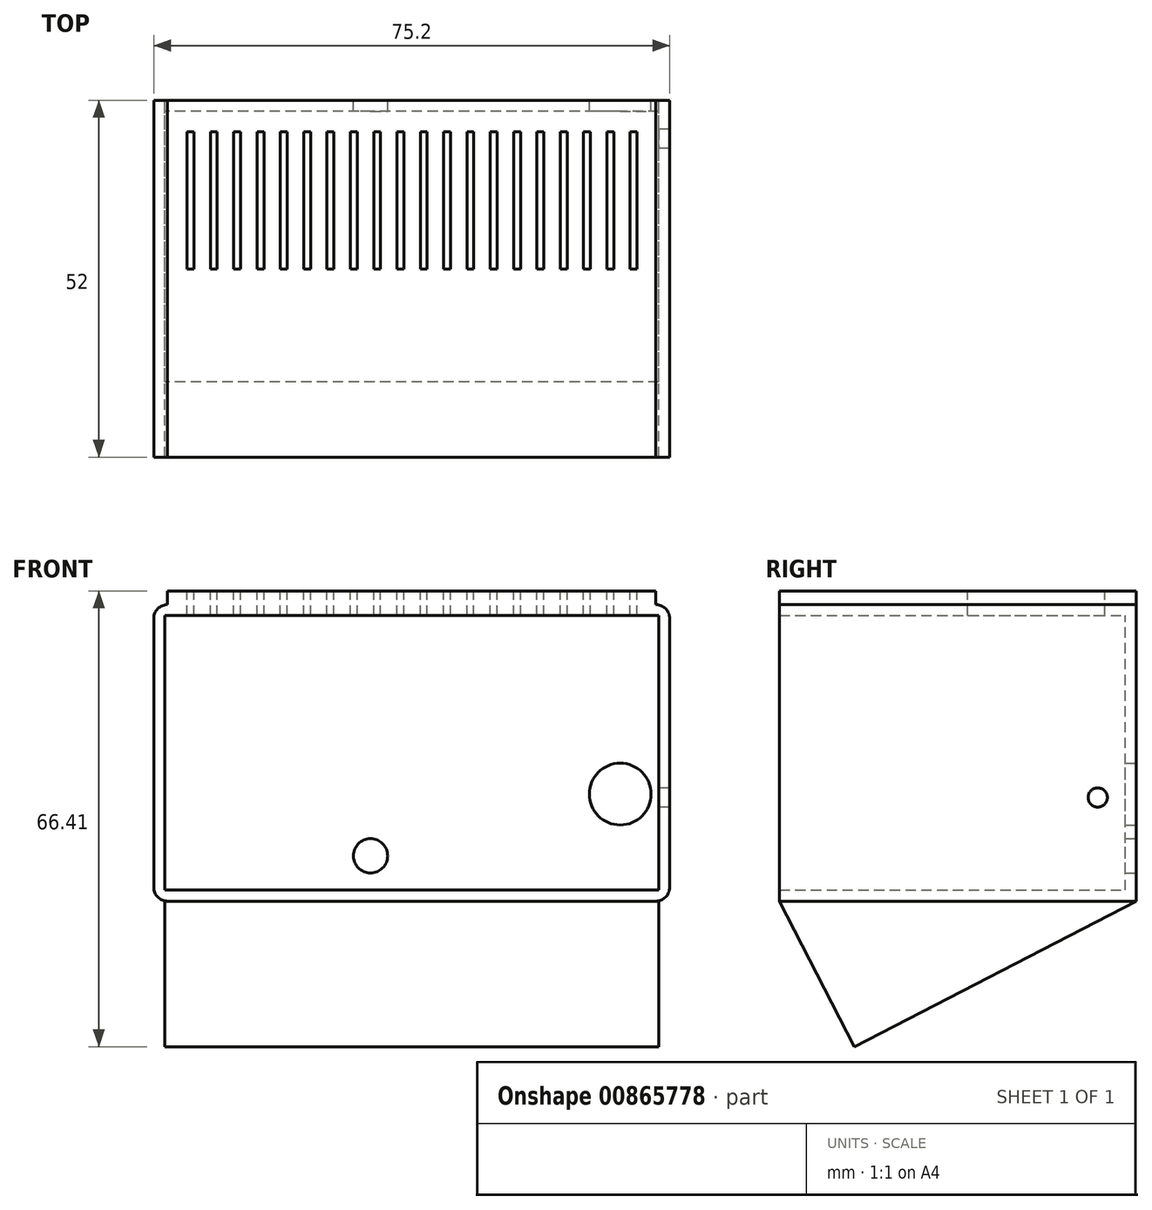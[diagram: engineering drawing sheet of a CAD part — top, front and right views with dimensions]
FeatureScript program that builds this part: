
annotation { "Feature Type Name" : "Feature", "Feature Type Description" : "" }
export const myFeature = defineFeature(function(context is Context, id is Id, definition is map)
    precondition{}
    {
        {
            var Q0;
            Q0=qCreatedBy(makeId("Front.planeOp"),FACE);
            var sketch = newSketch(context, id + "F0", { "sketchPlane" : qUnion([Q0])});
            skLineSegment(sketch, "E0.bottom", {"start": v(36, -20) * mm, "end": v(-36, -20) * mm});
            skLineSegment(sketch, "E0.top", {"start": v(36, 20) * mm, "end": v(-36, 20) * mm});
            skLineSegment(sketch, "E0.left", {"start": v(36, -20) * mm, "end": v(36, 20) * mm});
            skLineSegment(sketch, "E0.right", {"start": v(-36, -20) * mm, "end": v(-36, 20) * mm});
            skPoint(sketch, "E0.middle", {"position": v(0, 0) * mm});
            skLineSegment(sketch, "E1.0", {"start": v(-37.6, -21.6) * mm, "end": v(-37.6, 21.6) * mm});
            skLineSegment(sketch, "E1.1", {"start": v(37.6, -21.6) * mm, "end": v(-37.6, -21.6) * mm});
            skLineSegment(sketch, "E1.2", {"start": v(37.6, -21.6) * mm, "end": v(37.6, 21.6) * mm});
            skLineSegment(sketch, "E1.3", {"start": v(37.6, 21.6) * mm, "end": v(-37.6, 21.6) * mm});
            skPoint(sketch, "E2", {"position": v(30.4, -6) * mm});
            skPoint(sketch, "E3", {"position": v(-6, -15) * mm});
            skSolve(sketch);
        }
        {
            var Q0;
            Q0=makeQuery(id+"F0.imprint","IMPRINT",FACE,{"disambiguationData":[TD([[makeQuery(id+"F0.imprint","IMPRINT",EDGE,{"derivedFrom":sQuery(id+"F0.wireOp",EDGE,"E0.bottom")}),1.0]])]});
            extrude(context, id + "F1", {"entities" : qUnion([Q0]), "depth" : 52 * mm, "offsetDistance" : 25 * mm});
        }
        {
            var Q0;
            Q0=makeQuery(id+"F1.opExtrude","SWEPT_EDGE",EDGE,{"disambiguationData":[OSD([sQuery(id+"F0.wireOp",EDGE,"E1.2"),sQuery(id+"F0.wireOp",EDGE,"E1.3")])]});
            var Q1;
            Q1=makeQuery(id+"F1.opExtrude","SWEPT_EDGE",EDGE,{"disambiguationData":[OSD([sQuery(id+"F0.wireOp",EDGE,"E1.0"),sQuery(id+"F0.wireOp",EDGE,"E1.3")])]});
            var Q2;
            Q2=makeQuery(id+"F1.opExtrude","SWEPT_EDGE",EDGE,{"disambiguationData":[OSD([sQuery(id+"F0.wireOp",EDGE,"E1.0"),sQuery(id+"F0.wireOp",EDGE,"E1.1")])]});
            var Q3;
            Q3=makeQuery(id+"F1.opExtrude","SWEPT_EDGE",EDGE,{"disambiguationData":[OSD([sQuery(id+"F0.wireOp",EDGE,"E1.1"),sQuery(id+"F0.wireOp",EDGE,"E1.2")])]});
            fillet(context, id + "F2", {"entities" : qUnion([Q0, Q1, Q2, Q3]), "radius" : 2 * mm, "tangentPropagation" : true, "allowEdgeOverflow" : false});
        }
        {
            var Q0;
            Q0=makeQuery(id+"F0.imprint","IMPRINT",FACE,{"disambiguationData":[TD([[makeQuery(id+"F0.imprint","IMPRINT",EDGE,{"derivedFrom":sQuery(id+"F0.wireOp",EDGE,"E0.bottom")}),-1.0]])]});
            extrude(context, id + "F3", {"entities" : qUnion([Q0]), "operationType" : NewBodyOperationType.ADD, "depth" : 1.6 * mm, "offsetDistance" : 25 * mm});
        }
        {
            var Q0;
            Q0=qCreatedBy(makeId("Right.planeOp"),FACE);
            var sketch = newSketch(context, id + "F4", { "sketchPlane" : qUnion([Q0])});
            skPoint(sketch, "E4.0", {"position": v(-52, -21.6) * mm});
            skLineSegment(sketch, "E5", {"start": v(-52, -21.6) * mm, "end": v(-41.04, -42.8) * mm});
            skLineSegment(sketch, "E6", {"start": v(-41.04, -42.8) * mm, "end": v(0, -21.6) * mm});
            skLineSegment(sketch, "E7", {"start": v(-52, -21.6) * mm, "end": v(0, -21.6) * mm});
            skSolve(sketch);
        }
        {
            var Q0;
            Q0=makeQuery(id+"F4.imprint","IMPRINT",FACE,{"disambiguationData":[TD([[makeQuery(id+"F4.imprint","IMPRINT",EDGE,{"derivedFrom":sQuery(id+"F4.wireOp",EDGE,"E5")}),1.0]])]});
            extrude(context, id + "F5", {"entities" : qUnion([Q0]), "operationType" : NewBodyOperationType.ADD, "endBound" : BoundingType.SYMMETRIC, "depth" : 72 * mm, "offsetDistance" : 25 * mm});
        }
        {
            var Q0;
            Q0=sQuery(id+"F0.wireOp",VERTEX,"E2");
            var Q1;
            Q1=makeQuery(id+"F1.opExtrude","SWEPT_BODY",BODY,{"disambiguationData":[OSD([sQuery(id+"F0.wireOp",EDGE,"E0.bottom"),sQuery(id+"F0.wireOp",EDGE,"E0.top"),sQuery(id+"F0.wireOp",EDGE,"E0.left"),sQuery(id+"F0.wireOp",EDGE,"E0.right"),sQuery(id+"F0.wireOp",EDGE,"E1.0"),sQuery(id+"F0.wireOp",EDGE,"E1.1"),sQuery(id+"F0.wireOp",EDGE,"E1.2"),sQuery(id+"F0.wireOp",EDGE,"E1.3")])]});
            hole(context, id + "F6", {"style" : HoleStyle.SIMPLE, "endStyle" : HoleEndStyle.THROUGH, "oppositeDirection" : true, "holeDiameter" : 9 * mm, "majorDiameter" : 5 * mm, "isTappedThrough" : true, "tappedDepth" : 12 * mm, "tapClearance" : 3, "locations" : qUnion([Q0]), "scope" : qUnion([Q1])});
        }
        {
            var Q0;
            Q0=makeQuery(id+"F1.opExtrude","SWEPT_FACE",FACE,{"disambiguationData":[OSD([sQuery(id+"F0.wireOp",EDGE,"E0.left")])]});
            var sketch = newSketch(context, id + "F7", { "sketchPlane" : qUnion([Q0])});
            skPoint(sketch, "E8", {"position": v(5.6, -6.5) * mm});
            skSolve(sketch);
        }
        {
            var Q0;
            Q0=sQuery(id+"F7.wireOp",VERTEX,"E8");
            var Q1;
            Q1=makeQuery(id+"F1.opExtrude","SWEPT_BODY",BODY,{"disambiguationData":[OSD([sQuery(id+"F0.wireOp",EDGE,"E0.bottom"),sQuery(id+"F0.wireOp",EDGE,"E0.top"),sQuery(id+"F0.wireOp",EDGE,"E0.left"),sQuery(id+"F0.wireOp",EDGE,"E0.right"),sQuery(id+"F0.wireOp",EDGE,"E1.0"),sQuery(id+"F0.wireOp",EDGE,"E1.1"),sQuery(id+"F0.wireOp",EDGE,"E1.2"),sQuery(id+"F0.wireOp",EDGE,"E1.3")])]});
            hole(context, id + "F8", {"style" : HoleStyle.SIMPLE, "endStyle" : HoleEndStyle.THROUGH, "holeDiameter" : 2.8 * mm, "majorDiameter" : 5 * mm, "isTappedThrough" : true, "tappedDepth" : 12 * mm, "tapClearance" : 3, "locations" : qUnion([Q0]), "scope" : qUnion([Q1])});
        }
        {
            var Q0;
            Q0=sQuery(id+"F0.wireOp",VERTEX,"E3");
            var Q1;
            Q1=makeQuery(id+"F1.opExtrude","SWEPT_BODY",BODY,{"disambiguationData":[OSD([sQuery(id+"F0.wireOp",EDGE,"E0.bottom"),sQuery(id+"F0.wireOp",EDGE,"E0.top"),sQuery(id+"F0.wireOp",EDGE,"E0.left"),sQuery(id+"F0.wireOp",EDGE,"E0.right"),sQuery(id+"F0.wireOp",EDGE,"E1.0"),sQuery(id+"F0.wireOp",EDGE,"E1.1"),sQuery(id+"F0.wireOp",EDGE,"E1.2"),sQuery(id+"F0.wireOp",EDGE,"E1.3")])]});
            hole(context, id + "F9", {"style" : HoleStyle.SIMPLE, "endStyle" : HoleEndStyle.THROUGH, "oppositeDirection" : true, "holeDiameter" : 5 * mm, "majorDiameter" : 5 * mm, "isTappedThrough" : true, "tappedDepth" : 12 * mm, "tapClearance" : 3, "locations" : qUnion([Q0]), "scope" : qUnion([Q1])});
        }
        {
            var Q0;
            Q0=makeQuery(id+"F1.opExtrude","SWEPT_FACE",FACE,{"disambiguationData":[OSD([sQuery(id+"F0.wireOp",EDGE,"E1.3")])]});
            var sketch = newSketch(context, id + "F10", { "sketchPlane" : qUnion([Q0])});
            skLineSegment(sketch, "E9.bottom", {"start": v(-32.74, -4.6) * mm, "end": v(-31.74, -4.6) * mm});
            skLineSegment(sketch, "E9.top", {"start": v(-32.74, -24.6) * mm, "end": v(-31.74, -24.6) * mm});
            skLineSegment(sketch, "E9.left", {"start": v(-32.74, -4.6) * mm, "end": v(-32.74, -24.6) * mm});
            skLineSegment(sketch, "E9.right", {"start": v(-31.74, -4.6) * mm, "end": v(-31.74, -24.6) * mm});
            skLineSegment(sketch, "E10.1.0.0", {"start": v(-29.34, -4.6) * mm, "end": v(-28.34, -4.6) * mm});
            skLineSegment(sketch, "E10.1.0.1", {"start": v(-29.34, -4.6) * mm, "end": v(-29.34, -24.6) * mm});
            skLineSegment(sketch, "E10.1.0.2", {"start": v(-28.34, -4.6) * mm, "end": v(-28.34, -24.6) * mm});
            skLineSegment(sketch, "E10.1.0.3", {"start": v(-29.34, -24.6) * mm, "end": v(-28.34, -24.6) * mm});
            skLineSegment(sketch, "E10.2.0.0", {"start": v(-25.94, -4.6) * mm, "end": v(-24.94, -4.6) * mm});
            skLineSegment(sketch, "E10.2.0.1", {"start": v(-25.94, -4.6) * mm, "end": v(-25.94, -24.6) * mm});
            skLineSegment(sketch, "E10.2.0.2", {"start": v(-24.94, -4.6) * mm, "end": v(-24.94, -24.6) * mm});
            skLineSegment(sketch, "E10.2.0.3", {"start": v(-25.94, -24.6) * mm, "end": v(-24.94, -24.6) * mm});
            skLineSegment(sketch, "E10.3.0.0", {"start": v(-22.54, -4.6) * mm, "end": v(-21.54, -4.6) * mm});
            skLineSegment(sketch, "E10.3.0.1", {"start": v(-22.54, -4.6) * mm, "end": v(-22.54, -24.6) * mm});
            skLineSegment(sketch, "E10.3.0.2", {"start": v(-21.54, -4.6) * mm, "end": v(-21.54, -24.6) * mm});
            skLineSegment(sketch, "E10.3.0.3", {"start": v(-22.54, -24.6) * mm, "end": v(-21.54, -24.6) * mm});
            skLineSegment(sketch, "E10.4.0.0", {"start": v(-19.14, -4.6) * mm, "end": v(-18.14, -4.6) * mm});
            skLineSegment(sketch, "E10.4.0.1", {"start": v(-19.14, -4.6) * mm, "end": v(-19.14, -24.6) * mm});
            skLineSegment(sketch, "E10.4.0.2", {"start": v(-18.14, -4.6) * mm, "end": v(-18.14, -24.6) * mm});
            skLineSegment(sketch, "E10.4.0.3", {"start": v(-19.14, -24.6) * mm, "end": v(-18.14, -24.6) * mm});
            skLineSegment(sketch, "E10.5.0.0", {"start": v(-15.74, -4.6) * mm, "end": v(-14.74, -4.6) * mm});
            skLineSegment(sketch, "E10.5.0.1", {"start": v(-15.74, -4.6) * mm, "end": v(-15.74, -24.6) * mm});
            skLineSegment(sketch, "E10.5.0.2", {"start": v(-14.74, -4.6) * mm, "end": v(-14.74, -24.6) * mm});
            skLineSegment(sketch, "E10.5.0.3", {"start": v(-15.74, -24.6) * mm, "end": v(-14.74, -24.6) * mm});
            skLineSegment(sketch, "E10.6.0.0", {"start": v(-12.34, -4.6) * mm, "end": v(-11.34, -4.6) * mm});
            skLineSegment(sketch, "E10.6.0.1", {"start": v(-12.34, -4.6) * mm, "end": v(-12.34, -24.6) * mm});
            skLineSegment(sketch, "E10.6.0.2", {"start": v(-11.34, -4.6) * mm, "end": v(-11.34, -24.6) * mm});
            skLineSegment(sketch, "E10.6.0.3", {"start": v(-12.34, -24.6) * mm, "end": v(-11.34, -24.6) * mm});
            skLineSegment(sketch, "E10.7.0.0", {"start": v(-8.94, -4.6) * mm, "end": v(-7.94, -4.6) * mm});
            skLineSegment(sketch, "E10.7.0.1", {"start": v(-8.94, -4.6) * mm, "end": v(-8.94, -24.6) * mm});
            skLineSegment(sketch, "E10.7.0.2", {"start": v(-7.94, -4.6) * mm, "end": v(-7.94, -24.6) * mm});
            skLineSegment(sketch, "E10.7.0.3", {"start": v(-8.94, -24.6) * mm, "end": v(-7.94, -24.6) * mm});
            skLineSegment(sketch, "E10.8.0.0", {"start": v(-5.54, -4.6) * mm, "end": v(-4.54, -4.6) * mm});
            skLineSegment(sketch, "E10.8.0.1", {"start": v(-5.54, -4.6) * mm, "end": v(-5.54, -24.6) * mm});
            skLineSegment(sketch, "E10.8.0.2", {"start": v(-4.54, -4.6) * mm, "end": v(-4.54, -24.6) * mm});
            skLineSegment(sketch, "E10.8.0.3", {"start": v(-5.54, -24.6) * mm, "end": v(-4.54, -24.6) * mm});
            skLineSegment(sketch, "E10.9.0.0", {"start": v(-2.14, -4.6) * mm, "end": v(-1.14, -4.6) * mm});
            skLineSegment(sketch, "E10.9.0.1", {"start": v(-2.14, -4.6) * mm, "end": v(-2.14, -24.6) * mm});
            skLineSegment(sketch, "E10.9.0.2", {"start": v(-1.14, -4.6) * mm, "end": v(-1.14, -24.6) * mm});
            skLineSegment(sketch, "E10.9.0.3", {"start": v(-2.14, -24.6) * mm, "end": v(-1.14, -24.6) * mm});
            skLineSegment(sketch, "E10.10.0.0", {"start": v(1.26, -4.6) * mm, "end": v(2.26, -4.6) * mm});
            skLineSegment(sketch, "E10.10.0.1", {"start": v(1.26, -4.6) * mm, "end": v(1.26, -24.6) * mm});
            skLineSegment(sketch, "E10.10.0.2", {"start": v(2.26, -4.6) * mm, "end": v(2.26, -24.6) * mm});
            skLineSegment(sketch, "E10.10.0.3", {"start": v(1.26, -24.6) * mm, "end": v(2.26, -24.6) * mm});
            skLineSegment(sketch, "E10.11.0.0", {"start": v(4.66, -4.6) * mm, "end": v(5.66, -4.6) * mm});
            skLineSegment(sketch, "E10.11.0.1", {"start": v(4.66, -4.6) * mm, "end": v(4.66, -24.6) * mm});
            skLineSegment(sketch, "E10.11.0.2", {"start": v(5.66, -4.6) * mm, "end": v(5.66, -24.6) * mm});
            skLineSegment(sketch, "E10.11.0.3", {"start": v(4.66, -24.6) * mm, "end": v(5.66, -24.6) * mm});
            skLineSegment(sketch, "E10.12.0.0", {"start": v(8.06, -4.6) * mm, "end": v(9.06, -4.6) * mm});
            skLineSegment(sketch, "E10.12.0.1", {"start": v(8.06, -4.6) * mm, "end": v(8.06, -24.6) * mm});
            skLineSegment(sketch, "E10.12.0.2", {"start": v(9.06, -4.6) * mm, "end": v(9.06, -24.6) * mm});
            skLineSegment(sketch, "E10.12.0.3", {"start": v(8.06, -24.6) * mm, "end": v(9.06, -24.6) * mm});
            skLineSegment(sketch, "E10.13.0.0", {"start": v(11.46, -4.6) * mm, "end": v(12.46, -4.6) * mm});
            skLineSegment(sketch, "E10.13.0.1", {"start": v(11.46, -4.6) * mm, "end": v(11.46, -24.6) * mm});
            skLineSegment(sketch, "E10.13.0.2", {"start": v(12.46, -4.6) * mm, "end": v(12.46, -24.6) * mm});
            skLineSegment(sketch, "E10.13.0.3", {"start": v(11.46, -24.6) * mm, "end": v(12.46, -24.6) * mm});
            skLineSegment(sketch, "E10.14.0.0", {"start": v(14.86, -4.6) * mm, "end": v(15.86, -4.6) * mm});
            skLineSegment(sketch, "E10.14.0.1", {"start": v(14.86, -4.6) * mm, "end": v(14.86, -24.6) * mm});
            skLineSegment(sketch, "E10.14.0.2", {"start": v(15.86, -4.6) * mm, "end": v(15.86, -24.6) * mm});
            skLineSegment(sketch, "E10.14.0.3", {"start": v(14.86, -24.6) * mm, "end": v(15.86, -24.6) * mm});
            skLineSegment(sketch, "E10.15.0.0", {"start": v(18.26, -4.6) * mm, "end": v(19.26, -4.6) * mm});
            skLineSegment(sketch, "E10.15.0.1", {"start": v(18.26, -4.6) * mm, "end": v(18.26, -24.6) * mm});
            skLineSegment(sketch, "E10.15.0.2", {"start": v(19.26, -4.6) * mm, "end": v(19.26, -24.6) * mm});
            skLineSegment(sketch, "E10.15.0.3", {"start": v(18.26, -24.6) * mm, "end": v(19.26, -24.6) * mm});
            skLineSegment(sketch, "E10.16.0.0", {"start": v(21.66, -4.6) * mm, "end": v(22.66, -4.6) * mm});
            skLineSegment(sketch, "E10.16.0.1", {"start": v(21.66, -4.6) * mm, "end": v(21.66, -24.6) * mm});
            skLineSegment(sketch, "E10.16.0.2", {"start": v(22.66, -4.6) * mm, "end": v(22.66, -24.6) * mm});
            skLineSegment(sketch, "E10.16.0.3", {"start": v(21.66, -24.6) * mm, "end": v(22.66, -24.6) * mm});
            skLineSegment(sketch, "E10.17.0.0", {"start": v(25.06, -4.6) * mm, "end": v(26.06, -4.6) * mm});
            skLineSegment(sketch, "E10.17.0.1", {"start": v(25.06, -4.6) * mm, "end": v(25.06, -24.6) * mm});
            skLineSegment(sketch, "E10.17.0.2", {"start": v(26.06, -4.6) * mm, "end": v(26.06, -24.6) * mm});
            skLineSegment(sketch, "E10.17.0.3", {"start": v(25.06, -24.6) * mm, "end": v(26.06, -24.6) * mm});
            skLineSegment(sketch, "E10.18.0.0", {"start": v(28.46, -4.6) * mm, "end": v(29.46, -4.6) * mm});
            skLineSegment(sketch, "E10.18.0.1", {"start": v(28.46, -4.6) * mm, "end": v(28.46, -24.6) * mm});
            skLineSegment(sketch, "E10.18.0.2", {"start": v(29.46, -4.6) * mm, "end": v(29.46, -24.6) * mm});
            skLineSegment(sketch, "E10.18.0.3", {"start": v(28.46, -24.6) * mm, "end": v(29.46, -24.6) * mm});
            skLineSegment(sketch, "E10.19.0.0", {"start": v(31.86, -4.6) * mm, "end": v(32.86, -4.6) * mm});
            skLineSegment(sketch, "E10.19.0.1", {"start": v(31.86, -4.6) * mm, "end": v(31.86, -24.6) * mm});
            skLineSegment(sketch, "E10.19.0.2", {"start": v(32.86, -4.6) * mm, "end": v(32.86, -24.6) * mm});
            skLineSegment(sketch, "E10.19.0.3", {"start": v(31.86, -24.6) * mm, "end": v(32.86, -24.6) * mm});
            skLineSegment(sketch, "E10.direction1", {"start": v(-32.74, -4.6) * mm, "end": v(-29.34, -4.6) * mm, "construction": true});
            skSolve(sketch);
        }
        {
            var Q0;
            Q0=makeQuery(id+"F10.imprint","IMPRINT",FACE,{"disambiguationData":[TD([[makeQuery(id+"F10.imprint","IMPRINT",EDGE,{"derivedFrom":sQuery(id+"F10.wireOp",EDGE,"E9.bottom")}),-1.0]])]});
            var Q1;
            Q1=makeQuery(id+"F10.imprint","IMPRINT",FACE,{"disambiguationData":[TD([[makeQuery(id+"F10.imprint","IMPRINT",EDGE,{"derivedFrom":sQuery(id+"F10.wireOp",EDGE,"E10.1.0.0")}),-1.0]])]});
            var Q2;
            Q2=makeQuery(id+"F10.imprint","IMPRINT",FACE,{"disambiguationData":[TD([[makeQuery(id+"F10.imprint","IMPRINT",EDGE,{"derivedFrom":sQuery(id+"F10.wireOp",EDGE,"E10.2.0.0")}),-1.0]])]});
            var Q3;
            Q3=makeQuery(id+"F10.imprint","IMPRINT",FACE,{"disambiguationData":[TD([[makeQuery(id+"F10.imprint","IMPRINT",EDGE,{"derivedFrom":sQuery(id+"F10.wireOp",EDGE,"E10.3.0.0")}),-1.0]])]});
            var Q4;
            Q4=makeQuery(id+"F10.imprint","IMPRINT",FACE,{"disambiguationData":[TD([[makeQuery(id+"F10.imprint","IMPRINT",EDGE,{"derivedFrom":sQuery(id+"F10.wireOp",EDGE,"E10.4.0.0")}),-1.0]])]});
            var Q5;
            Q5=makeQuery(id+"F10.imprint","IMPRINT",FACE,{"disambiguationData":[TD([[makeQuery(id+"F10.imprint","IMPRINT",EDGE,{"derivedFrom":sQuery(id+"F10.wireOp",EDGE,"E10.5.0.0")}),-1.0]])]});
            var Q6;
            Q6=makeQuery(id+"F10.imprint","IMPRINT",FACE,{"disambiguationData":[TD([[makeQuery(id+"F10.imprint","IMPRINT",EDGE,{"derivedFrom":sQuery(id+"F10.wireOp",EDGE,"E10.6.0.0")}),-1.0]])]});
            var Q7;
            Q7=makeQuery(id+"F10.imprint","IMPRINT",FACE,{"disambiguationData":[TD([[makeQuery(id+"F10.imprint","IMPRINT",EDGE,{"derivedFrom":sQuery(id+"F10.wireOp",EDGE,"E10.7.0.0")}),-1.0]])]});
            var Q8;
            Q8=makeQuery(id+"F10.imprint","IMPRINT",FACE,{"disambiguationData":[TD([[makeQuery(id+"F10.imprint","IMPRINT",EDGE,{"derivedFrom":sQuery(id+"F10.wireOp",EDGE,"E10.8.0.0")}),-1.0]])]});
            var Q9;
            Q9=makeQuery(id+"F10.imprint","IMPRINT",FACE,{"disambiguationData":[TD([[makeQuery(id+"F10.imprint","IMPRINT",EDGE,{"derivedFrom":sQuery(id+"F10.wireOp",EDGE,"E10.10.0.0")}),-1.0]])]});
            var Q10;
            Q10=makeQuery(id+"F10.imprint","IMPRINT",FACE,{"disambiguationData":[TD([[makeQuery(id+"F10.imprint","IMPRINT",EDGE,{"derivedFrom":sQuery(id+"F10.wireOp",EDGE,"E10.11.0.0")}),-1.0]])]});
            var Q11;
            Q11=makeQuery(id+"F10.imprint","IMPRINT",FACE,{"disambiguationData":[TD([[makeQuery(id+"F10.imprint","IMPRINT",EDGE,{"derivedFrom":sQuery(id+"F10.wireOp",EDGE,"E10.9.0.0")}),-1.0]])]});
            var Q12;
            Q12=makeQuery(id+"F10.imprint","IMPRINT",FACE,{"disambiguationData":[TD([[makeQuery(id+"F10.imprint","IMPRINT",EDGE,{"derivedFrom":sQuery(id+"F10.wireOp",EDGE,"E10.12.0.0")}),-1.0]])]});
            var Q13;
            Q13=makeQuery(id+"F10.imprint","IMPRINT",FACE,{"disambiguationData":[TD([[makeQuery(id+"F10.imprint","IMPRINT",EDGE,{"derivedFrom":sQuery(id+"F10.wireOp",EDGE,"E10.13.0.0")}),-1.0]])]});
            var Q14;
            Q14=makeQuery(id+"F10.imprint","IMPRINT",FACE,{"disambiguationData":[TD([[makeQuery(id+"F10.imprint","IMPRINT",EDGE,{"derivedFrom":sQuery(id+"F10.wireOp",EDGE,"E10.14.0.0")}),-1.0]])]});
            var Q15;
            Q15=makeQuery(id+"F10.imprint","IMPRINT",FACE,{"disambiguationData":[TD([[makeQuery(id+"F10.imprint","IMPRINT",EDGE,{"derivedFrom":sQuery(id+"F10.wireOp",EDGE,"E10.15.0.0")}),-1.0]])]});
            var Q16;
            Q16=makeQuery(id+"F10.imprint","IMPRINT",FACE,{"disambiguationData":[TD([[makeQuery(id+"F10.imprint","IMPRINT",EDGE,{"derivedFrom":sQuery(id+"F10.wireOp",EDGE,"E10.16.0.0")}),-1.0]])]});
            var Q17;
            Q17=makeQuery(id+"F10.imprint","IMPRINT",FACE,{"disambiguationData":[TD([[makeQuery(id+"F10.imprint","IMPRINT",EDGE,{"derivedFrom":sQuery(id+"F10.wireOp",EDGE,"E10.17.0.0")}),-1.0]])]});
            var Q18;
            Q18=makeQuery(id+"F10.imprint","IMPRINT",FACE,{"disambiguationData":[TD([[makeQuery(id+"F10.imprint","IMPRINT",EDGE,{"derivedFrom":sQuery(id+"F10.wireOp",EDGE,"E10.18.0.0")}),-1.0]])]});
            var Q19;
            Q19=makeQuery(id+"F10.imprint","IMPRINT",FACE,{"disambiguationData":[TD([[makeQuery(id+"F10.imprint","IMPRINT",EDGE,{"derivedFrom":sQuery(id+"F10.wireOp",EDGE,"E10.19.0.0")}),-1.0]])]});
            extrude(context, id + "F11", {"entities" : qUnion([Q0, Q1, Q2, Q3, Q4, Q5, Q6, Q7, Q8, Q9, Q10, Q11, Q12, Q13, Q14, Q15, Q16, Q17, Q18, Q19]), "operationType" : NewBodyOperationType.REMOVE, "oppositeDirection" : true, "depth" : 25 * mm, "offsetDistance" : 25 * mm});
        }
        {
            var Q0;
            Q0=makeQuery(id+"F1.opExtrude","SWEPT_FACE",FACE,{"disambiguationData":[OSD([sQuery(id+"F0.wireOp",EDGE,"E1.3")])]});
            extrude(context, id + "F12", {"entities" : qUnion([Q0]), "operationType" : NewBodyOperationType.ADD, "depth" : 2 * mm, "offsetDistance" : 25 * mm});
        }
    });
